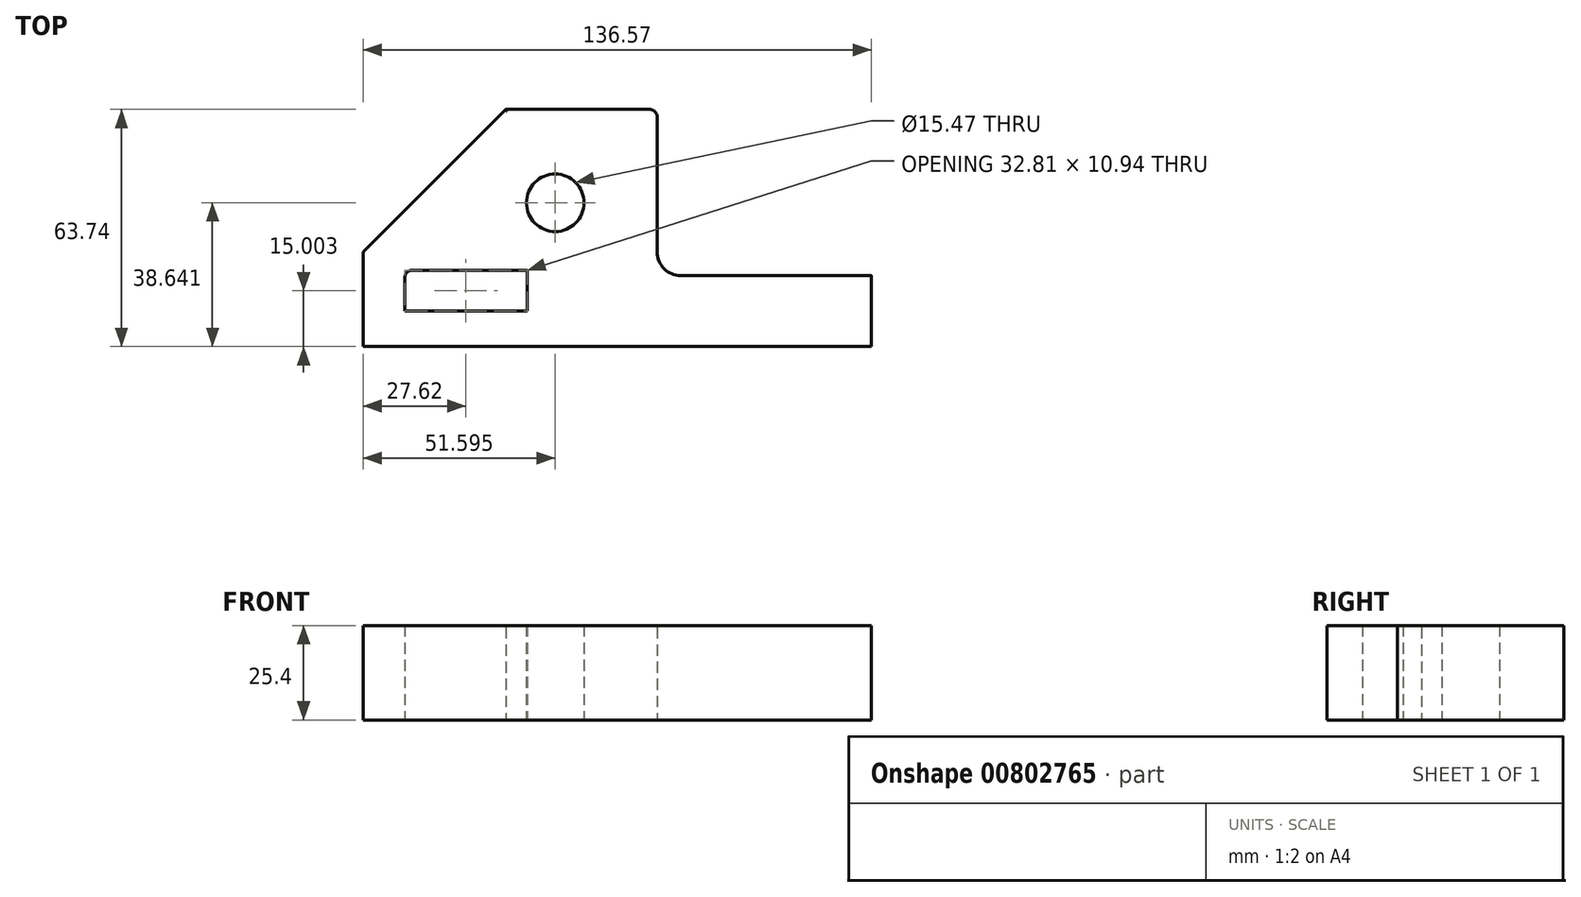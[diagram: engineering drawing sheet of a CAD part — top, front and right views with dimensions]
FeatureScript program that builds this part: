
annotation { "Feature Type Name" : "Feature", "Feature Type Description" : "" }
export const myFeature = defineFeature(function(context is Context, id is Id, definition is map)
    precondition{}
    {
        {
            var Q0;
            Q0=qCreatedBy(makeId("Top.planeOp"),FACE);
            var sketch = newSketch(context, id + "F0", { "sketchPlane" : qUnion([Q0])});
            skLineSegment(sketch, "E0", {"start": v(0, 0) * mm, "end": v(-110.16, 0) * mm});
            skLineSegment(sketch, "E1", {"start": v(-110.16, 0) * mm, "end": v(-110.16, 25.4) * mm});
            skLineSegment(sketch, "E2", {"start": v(-110.16, 25.4) * mm, "end": v(-71.82, 63.74) * mm});
            skLineSegment(sketch, "E3", {"start": v(-71.82, 63.74) * mm, "end": v(-31.17, 63.74) * mm});
            skLineSegment(sketch, "E4", {"start": v(-31.17, 63.74) * mm, "end": v(-31.17, 25.38) * mm});
            skLineSegment(sketch, "E5", {"start": v(-24.82, 19.03) * mm, "end": v(26.41, 19.03) * mm});
            skLineSegment(sketch, "E6", {"start": v(26.41, 19.03) * mm, "end": v(26.41, 0) * mm});
            skLineSegment(sketch, "E7", {"start": v(26.41, 0) * mm, "end": v(0, 0) * mm});
            skPoint(sketch, "E8.visualSharp", {"position": v(-31.17, 19.03) * mm});
            skArc(sketch, "E8.filletArc", {"start": v(-31.17, 25.38) * mm, "mid": v(-29.3, 20.9) * mm, "end": v(-24.82, 19.03) * mm});
            skCircle(sketch, "E9", {"center": v(-58.56, 38.64) * mm, "radius": 7.73 * mm});
            skLineSegment(sketch, "E10.bottom", {"start": v(-97.13, 20.47) * mm, "end": v(-66.14, 20.47) * mm});
            skLineSegment(sketch, "E10.top", {"start": v(-98.94, 9.54) * mm, "end": v(-66.14, 9.54) * mm});
            skLineSegment(sketch, "E10.left", {"start": v(-98.94, 18.66) * mm, "end": v(-98.94, 9.54) * mm});
            skLineSegment(sketch, "E10.right", {"start": v(-66.14, 20.47) * mm, "end": v(-66.14, 9.54) * mm});
            skPoint(sketch, "E11.visualSharp", {"position": v(-98.94, 20.47) * mm});
            skArc(sketch, "E11.filletArc", {"start": v(-97.13, 20.47) * mm, "mid": v(-98.41, 19.94) * mm, "end": v(-98.94, 18.66) * mm});
            skSolve(sketch);
        }
        {
            var Q0;
            Q0=makeQuery(id+"F0.imprint","IMPRINT",FACE,{"disambiguationData":[TD([[makeQuery(id+"F0.imprint","IMPRINT",EDGE,{"derivedFrom":sQuery(id+"F0.wireOp",EDGE,"E0")}),-1.0]])]});
            extrude(context, id + "F1", {"entities" : qUnion([Q0]), "depth" : 25.4 * mm, "offsetDistance" : 25.4 * mm});
        }
        {
            var Q0;
            Q0=makeQuery(id+"F1.opExtrude","SWEPT_EDGE",EDGE,{"disambiguationData":[OSD([sQuery(id+"F0.wireOp",EDGE,"E3"),sQuery(id+"F0.wireOp",EDGE,"E4")])]});
            fillet(context, id + "F2", {"entities" : qUnion([Q0]), "radius" : 2 * mm, "tangentPropagation" : true, "allowEdgeOverflow" : false});
        }
        {
            var Q0;
            Q0=makeQuery(id+"F1.opExtrude","CAP_EDGE",EDGE,{"disambiguationData":[OSD([sQuery(id+"F0.wireOp",EDGE,"E2")])],"isStart":false});
            var Q1;
            Q1=makeQuery(id+"F1.opExtrude","CAP_EDGE",EDGE,{"disambiguationData":[OSD([sQuery(id+"F0.wireOp",EDGE,"E3")])],"isStart":false});
            fillet(context, id + "F3", {"entities" : qUnion([Q0, Q1]), "radius" : 0.5 * mm, "tangentPropagation" : true, "allowEdgeOverflow" : false});
        }
    });
